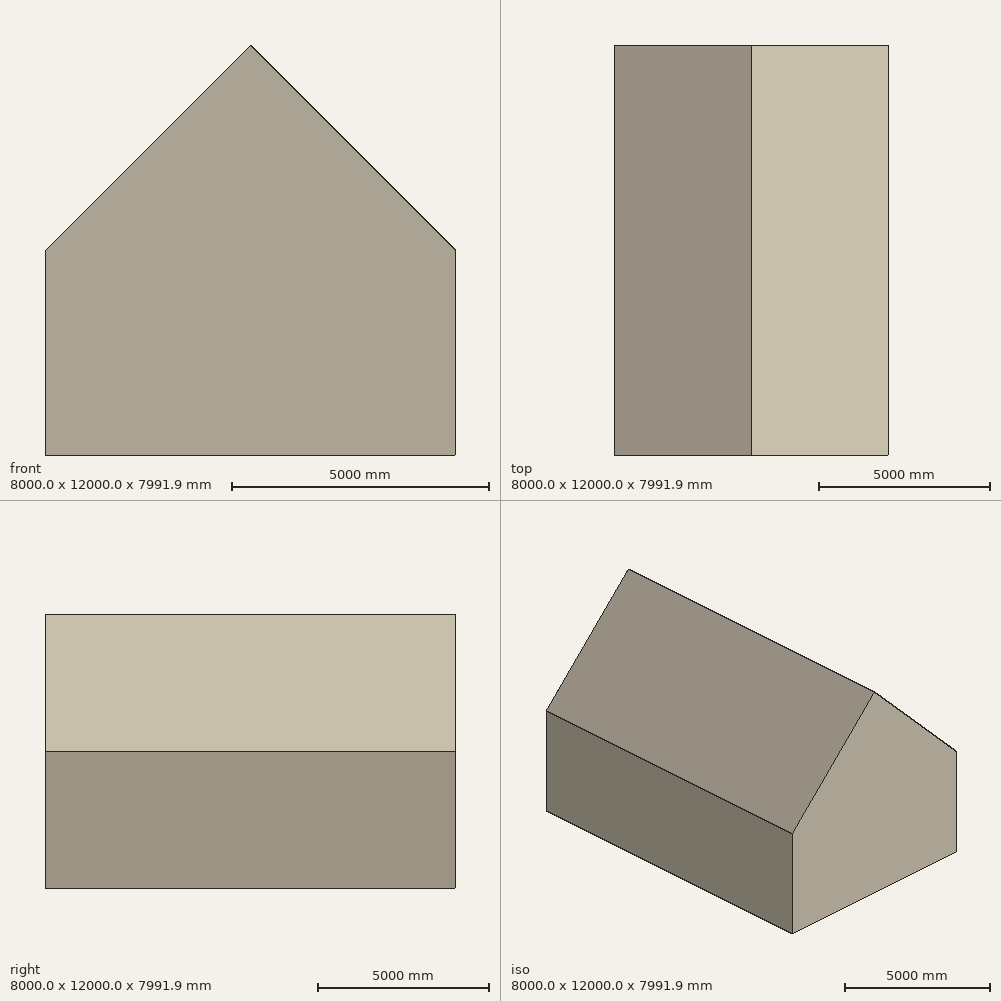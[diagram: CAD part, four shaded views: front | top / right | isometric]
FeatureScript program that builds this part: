
annotation { "Feature Type Name" : "Feature", "Feature Type Description" : "" }
export const myFeature = defineFeature(function(context is Context, id is Id, definition is map)
    precondition{}
    {
        {
            var Q0;
            Q0=qCreatedBy(makeId("Front.planeOp"),FACE);
            var sketch = newSketch(context, id + "F0", { "sketchPlane" : qUnion([Q0])});
            skLineSegment(sketch, "E0.bottom", {"start": v(-6030.7, 4016.29) * mm, "end": v(1969.3, 4016.29) * mm});
            skLineSegment(sketch, "E0.top", {"start": v(-6030.7, -3983.71) * mm, "end": v(1969.3, -3983.71) * mm});
            skLineSegment(sketch, "E0.left", {"start": v(-6030.7, 4016.29) * mm, "end": v(-6030.7, -3983.71) * mm});
            skLineSegment(sketch, "E0.right", {"start": v(1969.3, 4016.29) * mm, "end": v(1969.3, -3983.71) * mm});
            skSolve(sketch);
        }
        {
            var Q0;
            Q0 = qSketchRegion(id + "F0", true);
            extrude(context, id + "F1", {"entities" : qUnion([Q0]), "depth" : 12000 * mm});
        }
        {
            var Q0;
            Q0=makeQuery(id+"F1.opExtrude","CAP_FACE",FACE,{"disambiguationData":[OSD([sQuery(id+"F0.wireOp",EDGE,"E0.bottom"),sQuery(id+"F0.wireOp",EDGE,"E0.top"),sQuery(id+"F0.wireOp",EDGE,"E0.left"),sQuery(id+"F0.wireOp",EDGE,"E0.right")])],"isStart":true});
            var sketch = newSketch(context, id + "F2", { "sketchPlane" : qUnion([Q0])});
            skLineSegment(sketch, "E1", {"start": v(-1969.3, 16.29) * mm, "end": v(2022.56, 4008.14) * mm});
            skLineSegment(sketch, "E2", {"start": v(2022.56, 4008.14) * mm, "end": v(6030.7, 0) * mm});
            skSolve(sketch);
        }
        {
            var Q0;
            {var subQ3=sQuery(id+"F2.wireOp",EDGE,"E1");Q0=makeQuery(id+"F2.imprint","IMPRINT",FACE,{"disambiguationData":[TD([[makeQuery(id+"F2.imprint","IMPRINT",EDGE,{"derivedFrom":subQ3}),1.0]])]});}
            extrude(context, id + "F3", {"entities" : qUnion([Q0]), "operationType" : NewBodyOperationType.REMOVE, "endBound" : BoundingType.THROUGH_ALL, "oppositeDirection" : true, "depth" : 25 * mm});
        }
    });
